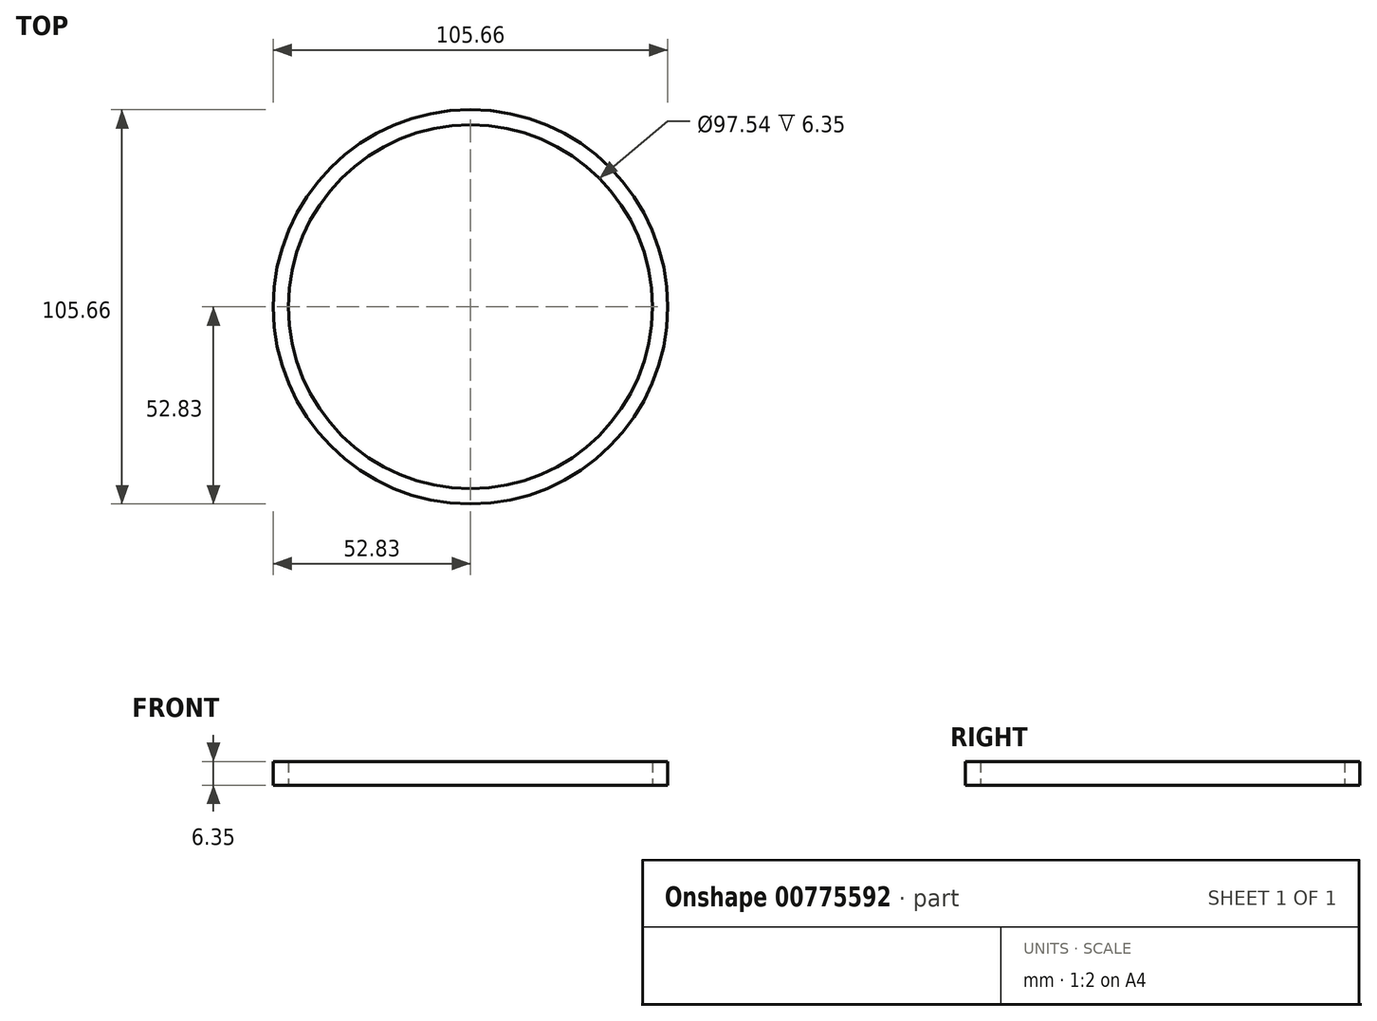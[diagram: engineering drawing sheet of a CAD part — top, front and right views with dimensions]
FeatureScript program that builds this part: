
annotation { "Feature Type Name" : "Feature", "Feature Type Description" : "" }
export const myFeature = defineFeature(function(context is Context, id is Id, definition is map)
    precondition{}
    {
        {
            var Q0;
            Q0=qCreatedBy(makeId("Top.planeOp"),FACE);
            var sketch = newSketch(context, id + "F0", { "sketchPlane" : qUnion([Q0])});
            skCircle(sketch, "E0", {"center": v(0, 0) * mm, "radius": 52.83 * mm});
            skCircle(sketch, "E1", {"center": v(0, 0) * mm, "radius": 48.77 * mm});
            skSolve(sketch);
        }
        {
            var Q0;
            Q0 = qSketchRegion(id + "F0", true);
            extrude(context, id + "F1", {"entities" : qUnion([Q0]), "depth" : 6.35 * mm, "offsetDistance" : 25.4 * mm});
        }
    });
